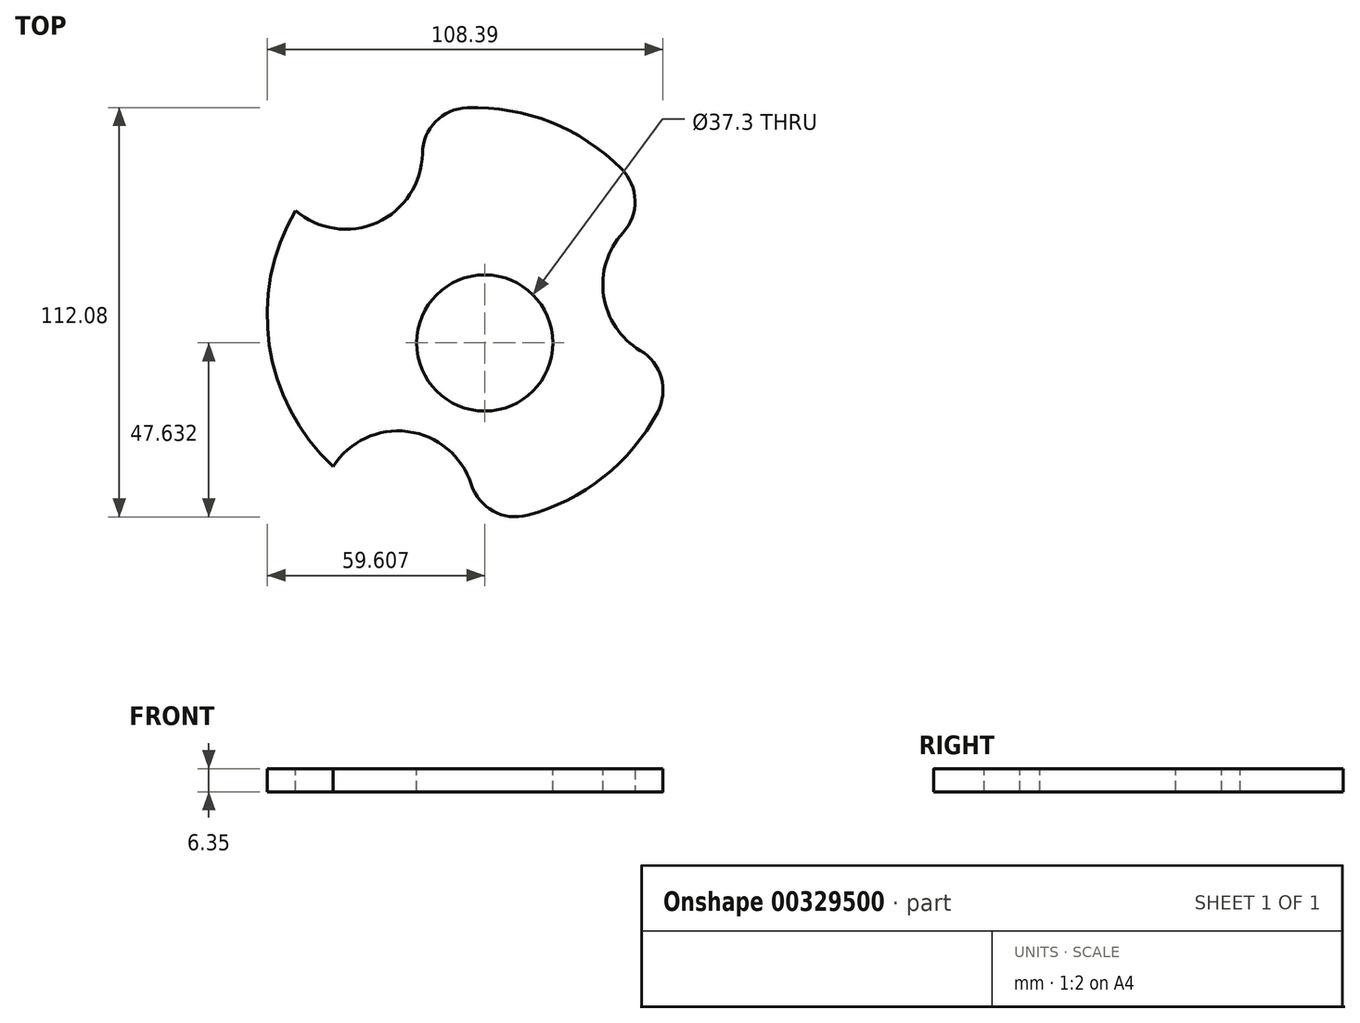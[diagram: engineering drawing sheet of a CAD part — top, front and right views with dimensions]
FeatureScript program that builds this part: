
annotation { "Feature Type Name" : "Feature", "Feature Type Description" : "" }
export const myFeature = defineFeature(function(context is Context, id is Id, definition is map)
    precondition{}
    {
        {
            var Q0;
            Q0=qCreatedBy(makeId("Top.planeOp"),FACE);
            var sketch = newSketch(context, id + "F0", { "sketchPlane" : qUnion([Q0])});
            skCircle(sketch, "E0", {"center": v(0, 0) * mm, "radius": 56.77 * mm});
            skSolve(sketch);
        }
        {
            var Q0;
            Q0=makeQuery(id+"F0.imprint","IMPRINT",FACE,{"disambiguationData":[TD([[makeQuery(id+"F0.imprint","IMPRINT",EDGE,{"derivedFrom":sQuery(id+"F0.wireOp",EDGE,"E0")}),1.0]])]});
            extrude(context, id + "F1", {"entities" : qUnion([Q0]), "depth" : 6.35 * mm});
        }
        {
            var Q0;
            Q0=makeQuery(id+"F1.opExtrude","CAP_FACE",FACE,{"disambiguationData":[OSD([sQuery(id+"F0.wireOp",EDGE,"E0")])],"isStart":false});
            var sketch = newSketch(context, id + "F2", { "sketchPlane" : qUnion([Q0])});
            skCircle(sketch, "E1", {"center": v(2.84, -7.68) * mm, "radius": 18.65 * mm});
            skSolve(sketch);
        }
        {
            var Q0;
            Q0 = qSketchRegion(id + "F2", true);
            extrude(context, id + "F3", {"entities" : qUnion([Q0]), "operationType" : NewBodyOperationType.REMOVE, "oppositeDirection" : true, "depth" : 25.4 * mm});
        }
        {
            var Q0;
            Q0=makeQuery(id+"F1.opExtrude","CAP_FACE",FACE,{"disambiguationData":[OSD([sQuery(id+"F0.wireOp",EDGE,"E0")])],"isStart":false});
            var sketch = newSketch(context, id + "F4", { "sketchPlane" : qUnion([Q0])});
            skArc(sketch, "E2", {"start": v(-49.03, 28.62) * mm, "mid": v(-22.21, 28.03) * mm, "end": v(-16.67, 54.27) * mm});
            skLineSegment(sketch, "E3", {"start": v(-49.03, 28.62) * mm, "end": v(-46.1, 60.05) * mm});
            skLineSegment(sketch, "E4", {"start": v(-46.1, 60.05) * mm, "end": v(-16.67, 54.27) * mm});
            skLineSegment(sketch, "E5.1.0", {"start": v(-0.27, -56.77) * mm, "end": v(-28.96, -69.95) * mm});
            skLineSegment(sketch, "E5.1.1", {"start": v(-28.96, -69.95) * mm, "end": v(-38.67, -41.57) * mm});
            skArc(sketch, "E5.1.2", {"start": v(-0.27, -56.77) * mm, "mid": v(-13.17, -33.25) * mm, "end": v(-38.67, -41.57) * mm});
            skLineSegment(sketch, "E5.2.0", {"start": v(49.3, 28.15) * mm, "end": v(75.06, 9.9) * mm});
            skLineSegment(sketch, "E5.2.1", {"start": v(75.06, 9.9) * mm, "end": v(55.33, -12.7) * mm});
            skArc(sketch, "E5.2.2", {"start": v(49.3, 28.15) * mm, "mid": v(35.38, 5.22) * mm, "end": v(55.33, -12.7) * mm});
            skPoint(sketch, "E5.center", {"position": v(0, 0) * mm});
            skSolve(sketch);
        }
        {
            var Q0;
            {var subQ0=sQuery(id+"F4.wireOp",EDGE,"E2");Q0=makeQuery(id+"F4.imprint","IMPRINT",FACE,{"disambiguationData":[TD([[makeQuery(id+"F4.imprint","IMPRINT",EDGE,{"derivedFrom":subQ0}),1.0]])]});}
            var Q1;
            {var subQ0=sQuery(id+"F4.wireOp",EDGE,"E5.2.2");Q1=makeQuery(id+"F4.imprint","IMPRINT",FACE,{"disambiguationData":[TD([[makeQuery(id+"F4.imprint","IMPRINT",EDGE,{"derivedFrom":subQ0}),1.0]])]});}
            var Q2;
            {var subQ0=sQuery(id+"F4.wireOp",EDGE,"E5.1.2");Q2=makeQuery(id+"F4.imprint","IMPRINT",FACE,{"disambiguationData":[TD([[makeQuery(id+"F4.imprint","IMPRINT",EDGE,{"derivedFrom":subQ0}),1.0]])]});}
            extrude(context, id + "F5", {"entities" : qUnion([Q0, Q1, Q2]), "operationType" : NewBodyOperationType.REMOVE, "oppositeDirection" : true, "depth" : 25.4 * mm});
        }
        {
            var Q0;
            Q0=makeQuery(id+"F5.boolean.opBoolean","COPY",EDGE,{"derivedFrom":makeQuery(id+"F5.opExtrude","SWEPT_EDGE",EDGE,{"disambiguationData":[OSD([sQuery(id+"F0.wireOp",EDGE,"E0"),sQuery(id+"F4.wireOp",EDGE,"E5.1.1"),sQuery(id+"F4.wireOp",EDGE,"E5.1.2")])]})});
            var Q1;
            Q1=makeQuery(id+"F5.boolean.opBoolean","COPY",EDGE,{"derivedFrom":makeQuery(id+"F5.opExtrude","SWEPT_EDGE",EDGE,{"disambiguationData":[OSD([sQuery(id+"F0.wireOp",EDGE,"E0"),sQuery(id+"F4.wireOp",EDGE,"E5.1.0"),sQuery(id+"F4.wireOp",EDGE,"E5.1.2")])]})});
            var Q2;
            Q2=makeQuery(id+"F5.boolean.opBoolean","COPY",EDGE,{"derivedFrom":makeQuery(id+"F5.opExtrude","SWEPT_EDGE",EDGE,{"disambiguationData":[OSD([sQuery(id+"F0.wireOp",EDGE,"E0"),sQuery(id+"F4.wireOp",EDGE,"E5.2.1"),sQuery(id+"F4.wireOp",EDGE,"E5.2.2")])]})});
            var Q3;
            Q3=makeQuery(id+"F5.boolean.opBoolean","COPY",EDGE,{"derivedFrom":makeQuery(id+"F5.opExtrude","SWEPT_EDGE",EDGE,{"disambiguationData":[OSD([sQuery(id+"F0.wireOp",EDGE,"E0"),sQuery(id+"F4.wireOp",EDGE,"E5.2.0"),sQuery(id+"F4.wireOp",EDGE,"E5.2.2")])]})});
            var Q4;
            Q4=makeQuery(id+"F5.boolean.opBoolean","COPY",EDGE,{"derivedFrom":makeQuery(id+"F5.opExtrude","SWEPT_EDGE",EDGE,{"disambiguationData":[OSD([sQuery(id+"F0.wireOp",EDGE,"E0"),sQuery(id+"F4.wireOp",EDGE,"E2"),sQuery(id+"F4.wireOp",EDGE,"E3")])]})});
            var Q5;
            Q5=makeQuery(id+"F5.boolean.opBoolean","COPY",EDGE,{"derivedFrom":makeQuery(id+"F5.opExtrude","SWEPT_EDGE",EDGE,{"disambiguationData":[OSD([sQuery(id+"F0.wireOp",EDGE,"E0"),sQuery(id+"F4.wireOp",EDGE,"E2"),sQuery(id+"F4.wireOp",EDGE,"E4")])]})});
            fillet(context, id + "F6", {"entities" : qUnion([Q0, Q1, Q2, Q3, Q4, Q5]), "radius" : 12.7 * mm, "tangentPropagation" : true, "allowEdgeOverflow" : false});
        }
    });
